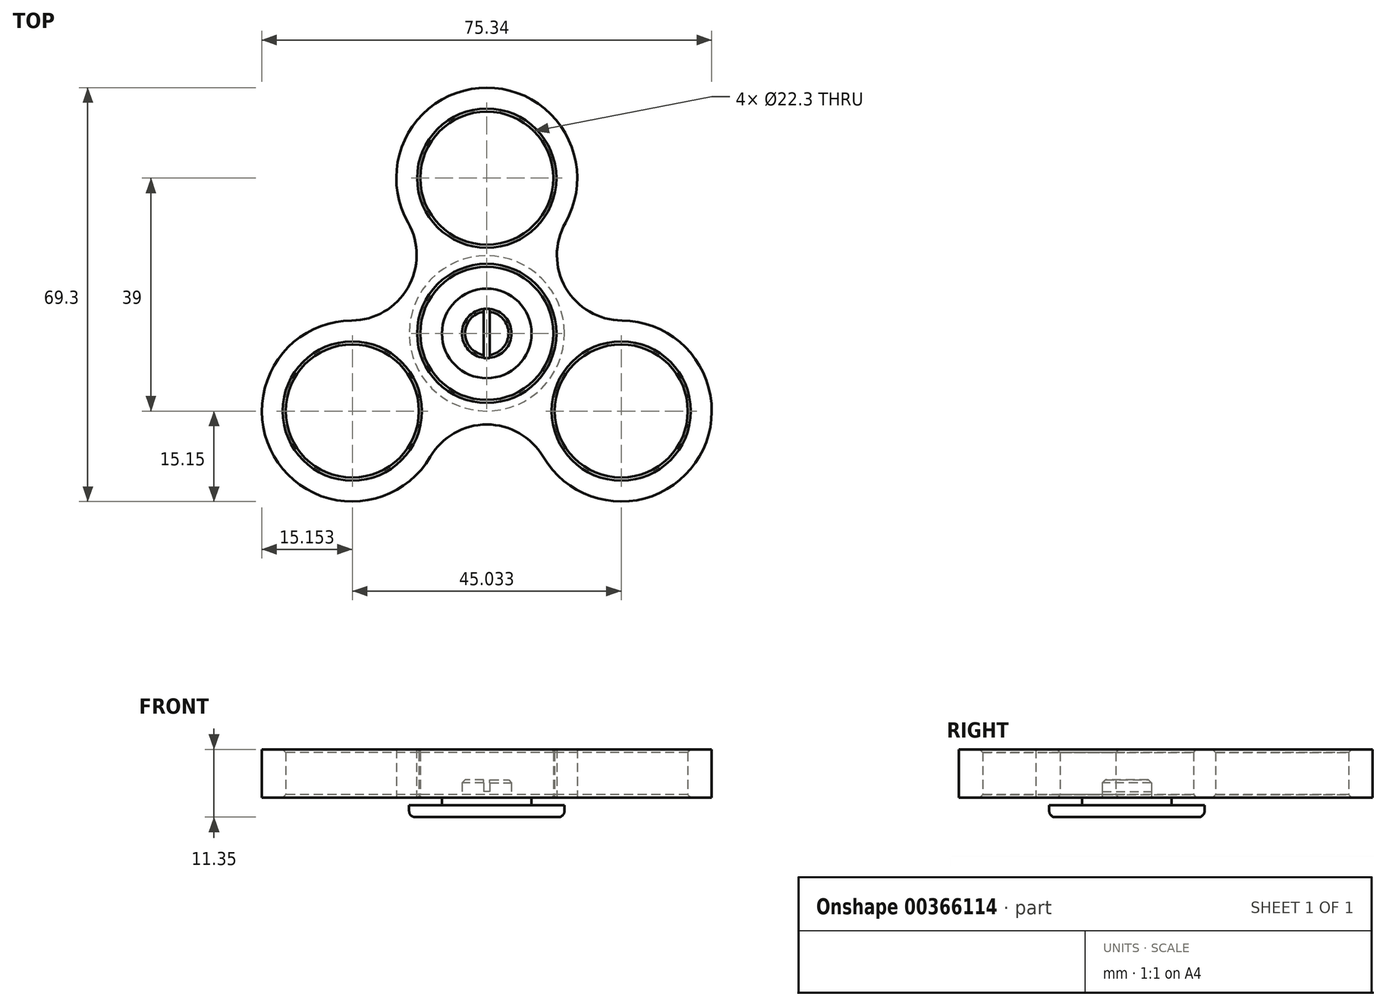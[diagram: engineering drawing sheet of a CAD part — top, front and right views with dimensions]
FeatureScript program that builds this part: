
annotation { "Feature Type Name" : "Feature", "Feature Type Description" : "" }
export const myFeature = defineFeature(function(context is Context, id is Id, definition is map)
    precondition{}
    {
        {
            var Q0;
            Q0=qCreatedBy(makeId("Top.planeOp"),FACE);
            var sketch = newSketch(context, id + "F0", { "sketchPlane" : qUnion([Q0])});
            skCircle(sketch, "E0", {"center": v(0, 0) * mm, "radius": 11.15 * mm});
            skCircle(sketch, "E1", {"center": v(0, 26) * mm, "radius": 11.15 * mm});
            skArc(sketch, "E2.0", {"start": v(13.17, 18.52) * mm, "mid": v(0, 41.15) * mm, "end": v(-13.17, 18.52) * mm});
            skCircle(sketch, "E3.1.0", {"center": v(-22.52, -13) * mm, "radius": 11.15 * mm});
            skArc(sketch, "E3.1.1", {"start": v(-22.63, 2.15) * mm, "mid": v(-35.64, -20.58) * mm, "end": v(-9.45, -20.67) * mm});
            skCircle(sketch, "E3.2.0", {"center": v(22.52, -13) * mm, "radius": 11.15 * mm});
            skArc(sketch, "E3.2.1", {"start": v(9.45, -20.67) * mm, "mid": v(35.64, -20.58) * mm, "end": v(22.63, 2.15) * mm});
            skArc(sketch, "E4", {"start": v(13.17, 18.52) * mm, "mid": v(13.21, 7.63) * mm, "end": v(22.63, 2.15) * mm});
            skArc(sketch, "E5.1.0", {"start": v(-22.63, 2.15) * mm, "mid": v(-13.21, 7.63) * mm, "end": v(-13.17, 18.52) * mm});
            skArc(sketch, "E5.2.0", {"start": v(9.45, -20.67) * mm, "mid": v(0, -15.26) * mm, "end": v(-9.45, -20.67) * mm});
            skSolve(sketch);
        }
        {
            var Q0;
            Q0 = qSketchRegion(id + "F0", true);
            extrude(context, id + "F1", {"entities" : qUnion([Q0]), "depth" : 8.1 * mm});
        }
        {
            var Q0;
            Q0=makeQuery(id+"F1.opExtrude","CAP_EDGE",EDGE,{"disambiguationData":[OSD([sQuery(id+"F0.wireOp",EDGE,"d6bf773e-89a3-495b-a429-f2a7d5ffcced.1.0")])],"isStart":false});
            var Q1;
            Q1=makeQuery(id+"F1.opExtrude","CAP_EDGE",EDGE,{"disambiguationData":[OSD([sQuery(id+"F0.wireOp",EDGE,"E0")])],"isStart":false});
            var Q2;
            Q2=makeQuery(id+"F1.opExtrude","CAP_EDGE",EDGE,{"disambiguationData":[OSD([sQuery(id+"F0.wireOp",EDGE,"E1")])],"isStart":false});
            var Q3;
            Q3=makeQuery(id+"F1.opExtrude","CAP_EDGE",EDGE,{"disambiguationData":[OSD([sQuery(id+"F0.wireOp",EDGE,"d6bf773e-89a3-495b-a429-f2a7d5ffcced.2.0")])],"isStart":false});
            var Q4;
            Q4=makeQuery(id+"F1.opExtrude","CAP_EDGE",EDGE,{"disambiguationData":[OSD([sQuery(id+"F0.wireOp",EDGE,"d6bf773e-89a3-495b-a429-f2a7d5ffcced.2.0")])],"isStart":true});
            var Q5;
            Q5=makeQuery(id+"F1.opExtrude","CAP_EDGE",EDGE,{"disambiguationData":[OSD([sQuery(id+"F0.wireOp",EDGE,"d6bf773e-89a3-495b-a429-f2a7d5ffcced.1.0")])],"isStart":true});
            var Q6;
            Q6=makeQuery(id+"F1.opExtrude","CAP_EDGE",EDGE,{"disambiguationData":[OSD([sQuery(id+"F0.wireOp",EDGE,"E1")])],"isStart":true});
            var Q7;
            Q7=makeQuery(id+"F1.opExtrude","CAP_EDGE",EDGE,{"disambiguationData":[OSD([sQuery(id+"F0.wireOp",EDGE,"E0")])],"isStart":true});
            var Q8;
            Q8=makeQuery(id+"F1.opExtrude","CAP_EDGE",EDGE,{"disambiguationData":[OSD([sQuery(id+"F0.wireOp",EDGE,"E3.2.0")])],"isStart":false});
            var Q9;
            Q9=makeQuery(id+"F1.opExtrude","CAP_EDGE",EDGE,{"disambiguationData":[OSD([sQuery(id+"F0.wireOp",EDGE,"E3.1.0")])],"isStart":false});
            var Q10;
            Q10=makeQuery(id+"F1.opExtrude","CAP_EDGE",EDGE,{"disambiguationData":[OSD([sQuery(id+"F0.wireOp",EDGE,"E3.1.0")])],"isStart":true});
            var Q11;
            Q11=makeQuery(id+"F1.opExtrude","CAP_EDGE",EDGE,{"disambiguationData":[OSD([sQuery(id+"F0.wireOp",EDGE,"E3.2.0")])],"isStart":true});
            chamfer(context, id + "F2", {"entities" : qUnion([Q0, Q1, Q2, Q3, Q4, Q5, Q6, Q7, Q8, Q9, Q10, Q11]), "width" : .5 * mm, "tangentPropagation" : true});
        }
        {
            var Q0;
            Q0=qCreatedBy(makeId("Top.planeOp"),FACE);
            var sketch = newSketch(context, id + "F3", { "sketchPlane" : qUnion([Q0])});
            skCircle(sketch, "E6", {"center": v(0, 0) * mm, "radius": 4.14 * mm});
            skSolve(sketch);
        }
        {
            var Q0;
            Q0 = qSketchRegion(id + "F3", true);
            extrude(context, id + "F4", {"entities" : qUnion([Q0]), "depth" : 3 * mm, "offsetDistance" : 25 * mm});
        }
        {
            var Q0;
            Q0=makeQuery(id+"F4.opExtrude","CAP_FACE",FACE,{"disambiguationData":[OSD([sQuery(id+"F3.wireOp",EDGE,"E6")])],"isStart":true});
            var sketch = newSketch(context, id + "F5", { "sketchPlane" : qUnion([Q0])});
            skCircle(sketch, "E7", {"center": v(0, 0) * mm, "radius": 7.5 * mm});
            skSolve(sketch);
        }
        {
            var Q0;
            Q0 = qSketchRegion(id + "F5", true);
            extrude(context, id + "F6", {"entities" : qUnion([Q0]), "operationType" : NewBodyOperationType.ADD, "depth" : 1.25 * mm, "offsetDistance" : 25 * mm});
        }
        {
            var Q0;
            Q0=makeQuery(id+"F6.opExtrude","CAP_FACE",FACE,{"disambiguationData":[OSD([sQuery(id+"F5.wireOp",EDGE,"E7")])],"isStart":false});
            var sketch = newSketch(context, id + "F7", { "sketchPlane" : qUnion([Q0])});
            skCircle(sketch, "E8", {"center": v(0, 0) * mm, "radius": 13 * mm});
            skSolve(sketch);
        }
        {
            var Q0;
            Q0 = qSketchRegion(id + "F7", true);
            extrude(context, id + "F8", {"entities" : qUnion([Q0]), "operationType" : NewBodyOperationType.ADD, "depth" : 2 * mm, "offsetDistance" : 25 * mm});
        }
        {
            var Q0;
            Q0=makeQuery(id+"F8.opExtrude","CAP_EDGE",EDGE,{"disambiguationData":[OSD([sQuery(id+"F7.wireOp",EDGE,"E8")])],"isStart":false});
            fillet(context, id + "F9", {"entities" : qUnion([Q0]), "radius" : 1 * mm, "tangentPropagation" : true, "allowEdgeOverflow" : false});
        }
        {
            var Q0;
            Q0=makeQuery(id+"F4.opExtrude","CAP_EDGE",EDGE,{"disambiguationData":[OSD([sQuery(id+"F3.wireOp",EDGE,"E6")])],"isStart":false});
            chamfer(context, id + "F10", {"entities" : qUnion([Q0]), "width" : .5 * mm, "tangentPropagation" : true});
        }
        {
            var Q0;
            Q0=makeQuery(id+"F4.opExtrude","CAP_FACE",FACE,{"disambiguationData":[OSD([sQuery(id+"F3.wireOp",EDGE,"E6")])],"isStart":false});
            var sketch = newSketch(context, id + "F11", { "sketchPlane" : qUnion([Q0])});
            skLineSegment(sketch, "E9.0", {"start": v(0.5, -4.95) * mm, "end": v(0.5, 5.3) * mm});
            skLineSegment(sketch, "E10.MirrorCS", {"start": v(-0.5, -4.95) * mm, "end": v(-0.5, 5.3) * mm});
            skLineSegment(sketch, "E11", {"start": v(-0.5, -4.95) * mm, "end": v(0.5, -4.95) * mm});
            skLineSegment(sketch, "E12", {"start": v(-0.5, 5.3) * mm, "end": v(0.5, 5.3) * mm});
            skSolve(sketch);
        }
        {
            var Q0;
            Q0 = qSketchRegion(id + "F11", true);
            extrude(context, id + "F12", {"entities" : qUnion([Q0]), "operationType" : NewBodyOperationType.REMOVE, "oppositeDirection" : true, "depth" : 2 * mm, "offsetDistance" : 25 * mm});
        }
    });
